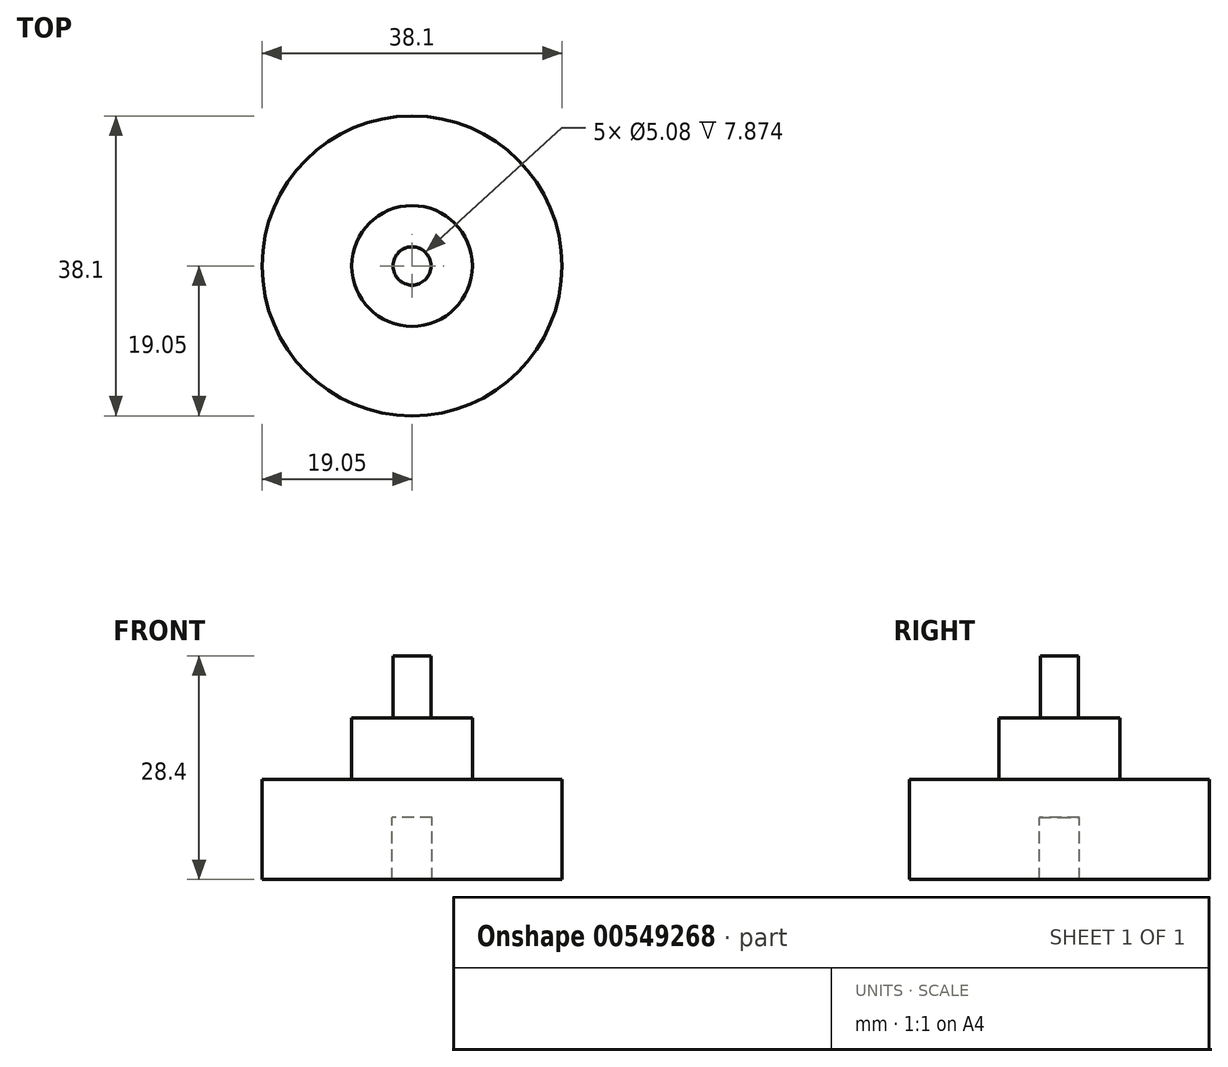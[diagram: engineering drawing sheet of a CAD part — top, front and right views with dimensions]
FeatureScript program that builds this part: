
annotation { "Feature Type Name" : "Feature", "Feature Type Description" : "" }
export const myFeature = defineFeature(function(context is Context, id is Id, definition is map)
    precondition{}
    {
        {
            var Q0;
            Q0=qCreatedBy(makeId("Front.planeOp"),FACE);
            var sketch = newSketch(context, id + "F0", { "sketchPlane" : qUnion([Q0])});
            skLineSegment(sketch, "E0", {"start": v(19.05, 0) * mm, "end": v(19.05, 12.7) * mm});
            skLineSegment(sketch, "E1", {"start": v(19.05, 12.7) * mm, "end": v(7.67, 12.7) * mm});
            skLineSegment(sketch, "E2", {"start": v(2.41, 20.55) * mm, "end": v(7.67, 20.55) * mm});
            skLineSegment(sketch, "E3", {"start": v(7.67, 20.55) * mm, "end": v(7.67, 12.7) * mm});
            skLineSegment(sketch, "E4", {"start": v(0, 28.4) * mm, "end": v(2.41, 28.4) * mm});
            skLineSegment(sketch, "E5", {"start": v(2.41, 28.4) * mm, "end": v(2.41, 20.55) * mm});
            skPoint(sketch, "E6.start.orphan", {"position": v(0, 12.7) * mm});
            skLineSegment(sketch, "E7", {"start": v(2.54, 0) * mm, "end": v(2.54, 7.87) * mm});
            skLineSegment(sketch, "E8", {"start": v(2.54, 7.87) * mm, "end": v(0, 7.87) * mm});
            skLineSegment(sketch, "E9", {"start": v(2.54, 0) * mm, "end": v(19.05, 0) * mm});
            skLineSegment(sketch, "E10", {"start": v(0, 28.4) * mm, "end": v(0, 7.87) * mm});
            skSolve(sketch);
        }
        {
            var Q0;
            Q0 = qSketchRegion(id + "F0", true);
            var Q1;
            Q1=sQuery(id+"F0.wireOp",EDGE,"E10");
            revolve(context, id + "F1", {"entities" : qUnion([Q0]), "axis" : qUnion([Q1]), "revolveType" : RevolveType.FULL});
        }
    });
